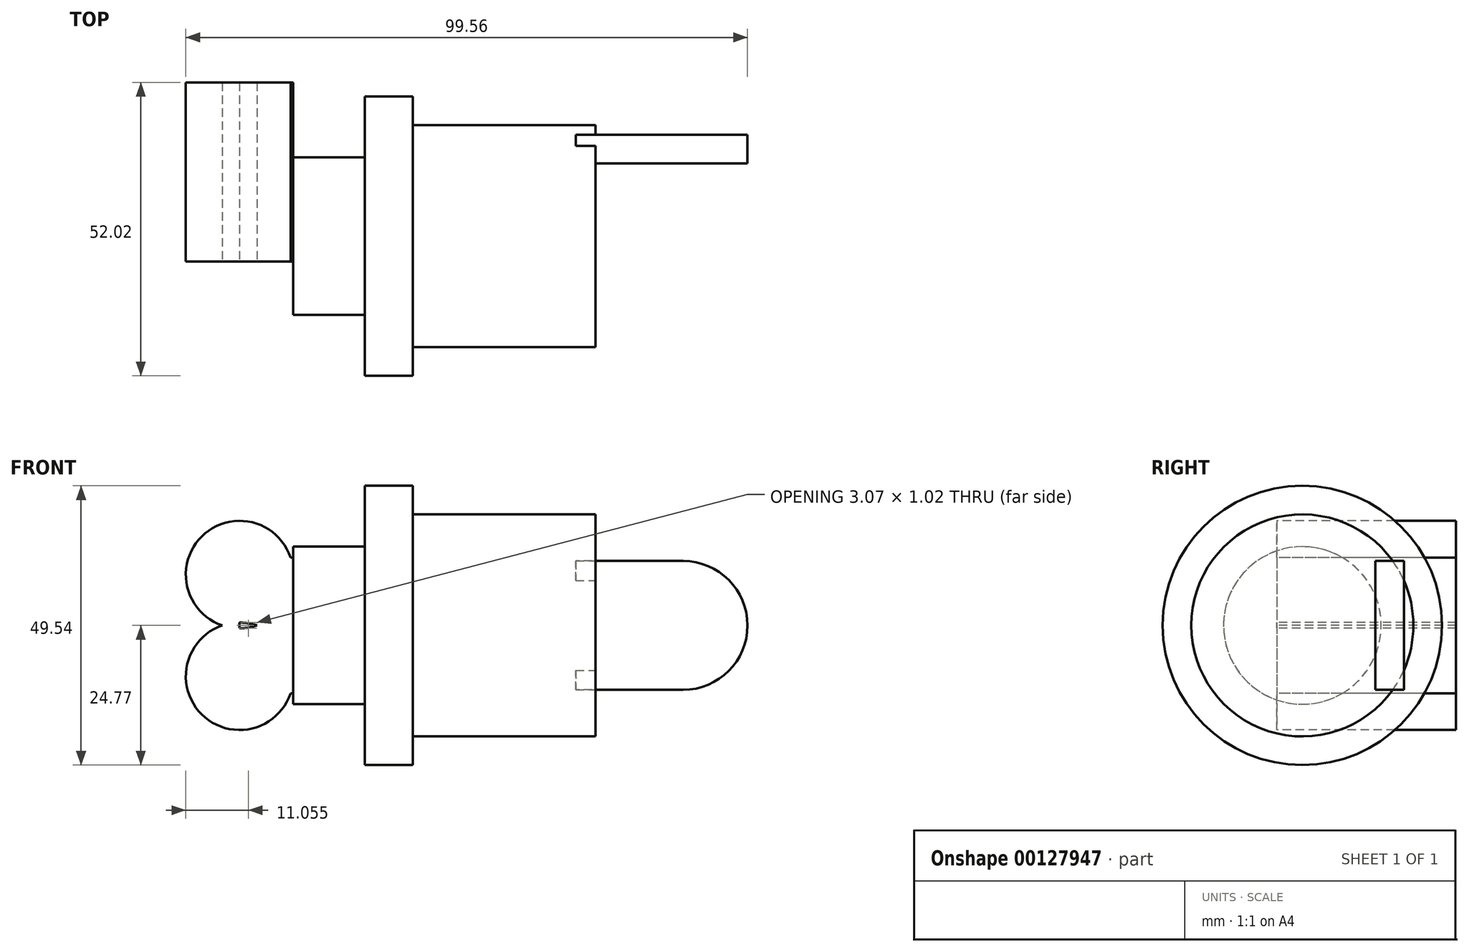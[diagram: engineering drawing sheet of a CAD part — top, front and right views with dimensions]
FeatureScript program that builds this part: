
annotation { "Feature Type Name" : "Feature", "Feature Type Description" : "" }
export const myFeature = defineFeature(function(context is Context, id is Id, definition is map)
    precondition{}
    {
        {
            var Q0;
            Q0=qCreatedBy(makeId("Front.planeOp"),FACE);
            var sketch = newSketch(context, id + "F0", { "sketchPlane" : qUnion([Q0])});
            skCircle(sketch, "E0", {"center": v(0, 0) * mm, "radius": 11.42 * mm});
            skSolve(sketch);
        }
        {
            var Q0;
            Q0=makeQuery(id+"F0.imprint","IMPRINT",FACE,{"disambiguationData":[TD([[makeQuery(id+"F0.imprint","IMPRINT",EDGE,{"derivedFrom":sQuery(id+"F0.wireOp",EDGE,"E0")}),1.0]])]});
            extrude(context, id + "F1", {"entities" : qUnion([Q0]), "depth" : 5.08 * mm});
        }
        {
            var Q0;
            Q0=qCreatedBy(makeId("Right.planeOp"),FACE);
            cPlane(context, id + "F2", {"entities" : qUnion([Q0]), "cplaneType" : CPlaneType.OFFSET, "offset" : 15.5 * mm, "oppositeDirection" : true, "width" : 152.4 * mm, "height" : 152.4 * mm});
        }
        {
            var Q0;
            Q0=qCreatedBy(id+"F2.planeOp",FACE);
            var sketch = newSketch(context, id + "F3", { "sketchPlane" : qUnion([Q0])});
            skCircle(sketch, "E1", {"center": v(-18, 0) * mm, "radius": 19.69 * mm});
            skSolve(sketch);
        }
        {
            var Q0;
            Q0=makeQuery(id+"F3.imprint","IMPRINT",FACE,{"disambiguationData":[TD([[makeQuery(id+"F3.imprint","IMPRINT",EDGE,{"derivedFrom":sQuery(id+"F3.wireOp",EDGE,"E1")}),1.0]])]});
            extrude(context, id + "F4", {"entities" : qUnion([Q0]), "oppositeDirection" : true, "depth" : 40.9 * mm});
        }
        {
            var Q0;
            Q0=makeQuery(id+"F1.opExtrude","CAP_FACE",FACE,{"disambiguationData":[OSD([sQuery(id+"F0.wireOp",EDGE,"E0")])],"isStart":true});
            var sketch = newSketch(context, id + "F5", { "sketchPlane" : qUnion([Q0])});
            skLineSegment(sketch, "E2.bottom", {"start": v(0, 11.42) * mm, "end": v(19.05, 11.42) * mm});
            skLineSegment(sketch, "E2.top", {"start": v(0, -11.42) * mm, "end": v(19.05, -11.42) * mm});
            skLineSegment(sketch, "E2.left", {"start": v(0, 11.42) * mm, "end": v(0, -11.42) * mm});
            skLineSegment(sketch, "E2.right", {"start": v(19.05, 11.42) * mm, "end": v(19.05, -11.42) * mm});
            skSolve(sketch);
        }
        {
            var Q0;
            {var subQ0=sQuery(id+"F5.wireOp",EDGE,"E2.bottom");Q0=makeQuery(id+"F5.imprint","IMPRINT",FACE,{"disambiguationData":[TD([[makeQuery(id+"F5.imprint","IMPRINT",EDGE,{"derivedFrom":subQ0}),-1.0]])]});}
            var Q1;
            Q1=makeQuery(id+"F1.opExtrude","CAP_FACE",FACE,{"disambiguationData":[OSD([sQuery(id+"F0.wireOp",EDGE,"E0")])],"isStart":false});
            extrude(context, id + "F6", {"entities" : qUnion([Q0]), "operationType" : NewBodyOperationType.ADD, "endBound" : BoundingType.UP_TO_SURFACE, "oppositeDirection" : true, "endBoundEntityFace" : qUnion([Q1]), "depth" : 25.4 * mm});
        }
        {
            var Q0;
            {var subQ0=sQuery(id+"F0.wireOp",EDGE,"E0");var subQ1=sQuery(id+"F3.wireOp",EDGE,"E1");Q0=makeQuery(id+"F6.boolean.opBoolean","SPLIT",FACE,{"disambiguationData":[TD([makeQuery(id+"F1.opExtrude","CAP_FACE",FACE,{"disambiguationData":[OSD([subQ0])],"isStart":false})])],"derivedFrom":makeQuery(id+"F4.opExtrude","CAP_FACE",FACE,{"disambiguationData":[OSD([subQ1])],"isStart":true})});}
            var sketch = newSketch(context, id + "F7", { "sketchPlane" : qUnion([Q0])});
            skPoint(sketch, "E3", {"position": v(-18, 0) * mm});
            skSolve(sketch);
        }
        {
            var Q0;
            Q0=qCreatedBy(makeId("Front.planeOp"),FACE);
            var Q1;
            Q1=sQuery(id+"F7.wireOp",VERTEX,"E3");
            cPlane(context, id + "F8", {"entities" : qUnion([Q0, Q1]), "cplaneType" : CPlaneType.PLANE_POINT, "offset" : 25.4 * mm, "width" : 152.4 * mm, "height" : 152.4 * mm});
        }
        {
            var Q0;
            Q0=makeQuery(id+"F4.opExtrude","CAP_FACE",FACE,{"disambiguationData":[OSD([sQuery(id+"F3.wireOp",EDGE,"E1")])],"isStart":false});
            var sketch = newSketch(context, id + "F9", { "sketchPlane" : qUnion([Q0])});
            skCircle(sketch, "E4", {"center": v(18, 0) * mm, "radius": 24.77 * mm});
            skSolve(sketch);
        }
        {
            var Q0;
            Q0 = qSketchRegion(id + "F9", true);
            var Q1;
            Q1 = qConstructionFilter(qBodyType(qCreatedBy(id + "F9" ,EDGE), BodyType.WIRE), ConstructionObject.NO);
            extrude(context, id + "F10", {"entities" : qUnion([Q0]), "operationType" : NewBodyOperationType.ADD, "surfaceEntities" : qUnion([Q1]), "oppositeDirection" : true, "depth" : 8.5 * mm});
        }
        {
            var Q0;
            Q0=makeQuery(id+"F10.boolean.opBoolean","MERGE",FACE,{"derivedFrom":[makeQuery(id+"F4.opExtrude","CAP_FACE",FACE,{"disambiguationData":[OSD([sQuery(id+"F3.wireOp",EDGE,"E1")])],"isStart":false}),makeQuery(id+"F10.opExtrude","CAP_FACE",FACE,{"disambiguationData":[OSD([sQuery(id+"F9.wireOp",EDGE,"E4")])],"isStart":true})]});
            var sketch = newSketch(context, id + "F11", { "sketchPlane" : qUnion([Q0])});
            skCircle(sketch, "E5", {"center": v(18, 0) * mm, "radius": 13.97 * mm});
            skSolve(sketch);
        }
        {
            var Q0;
            Q0 = qSketchRegion(id + "F11", true);
            extrude(context, id + "F12", {"entities" : qUnion([Q0]), "operationType" : NewBodyOperationType.ADD, "depth" : 12.7 * mm});
        }
        {
            var Q0;
            Q0=qCreatedBy(id+"F8.planeOp",FACE);
            cPlane(context, id + "F13", {"entities" : qUnion([Q0]), "cplaneType" : CPlaneType.OFFSET, "offset" : 4.5 * mm, "width" : 152.4 * mm, "height" : 152.4 * mm});
        }
        {
            var Q0;
            Q0=qCreatedBy(id+"F13.planeOp",FACE);
            var sketch = newSketch(context, id + "F14", { "sketchPlane" : qUnion([Q0])});
            skCircle(sketch, "E6", {"center": v(-78.62, 9.02) * mm, "radius": 9.52 * mm});
            skCircle(sketch, "E7", {"center": v(-78.62, -9.02) * mm, "radius": 9.52 * mm});
            skLineSegment(sketch, "E8", {"start": v(-78.62, 9.02) * mm, "end": v(-78.62, -9.02) * mm, "construction": true});
            skLineSegment(sketch, "E9.0", {"start": v(-69.1, -13.97) * mm, "end": v(-69.1, 13.97) * mm, "construction": true});
            skLineSegment(sketch, "E10", {"start": v(-78.62, 0) * mm, "end": v(-69.1, 0) * mm, "construction": true});
            skLineSegment(sketch, "E11", {"start": v(-69.58, 12.03) * mm, "end": v(-69.1, 12.03) * mm});
            skLineSegment(sketch, "E12", {"start": v(-69.1, 12.03) * mm, "end": v(-69.1, -12.03) * mm});
            skLineSegment(sketch, "E13", {"start": v(-69.1, -12.03) * mm, "end": v(-69.58, -12.03) * mm});
            skLineSegment(sketch, "E14", {"start": v(-69.58, -12.03) * mm, "end": v(-78.62, -12.03) * mm});
            skLineSegment(sketch, "E15", {"start": v(-78.62, -12.03) * mm, "end": v(-78.62, 12.03) * mm});
            skLineSegment(sketch, "E16", {"start": v(-78.62, 12.03) * mm, "end": v(-69.58, 12.03) * mm});
            skSolve(sketch);
        }
        {
            var Q0;
            Q0 = qSketchRegion(id + "F14", true);
            extrude(context, id + "F15", {"entities" : qUnion([Q0]), "operationType" : NewBodyOperationType.ADD, "oppositeDirection" : true, "depth" : 31.75 * mm});
        }
    });
